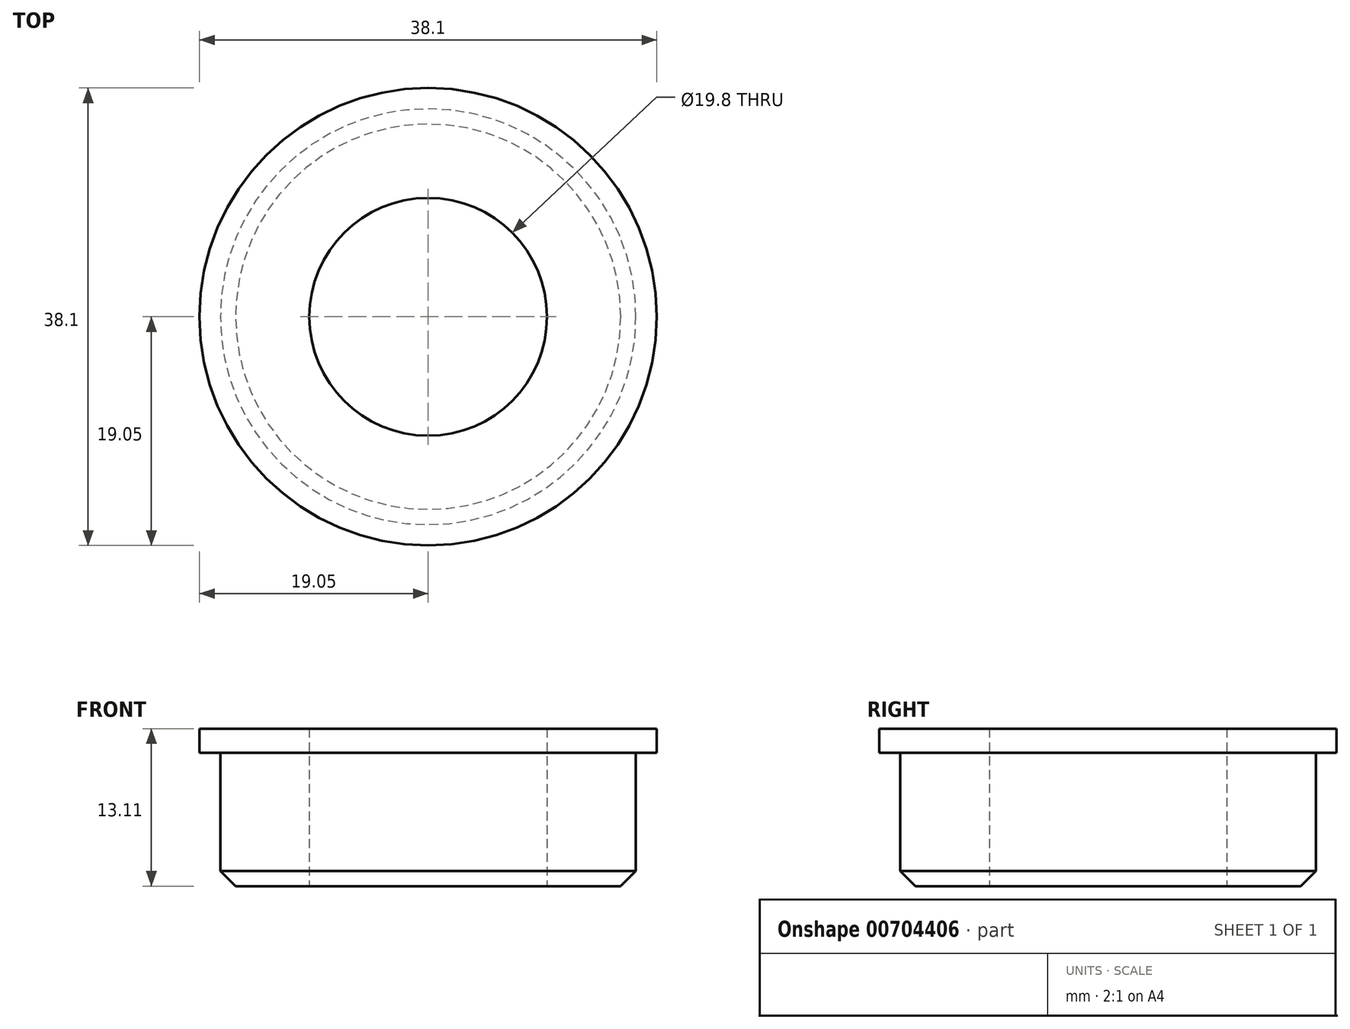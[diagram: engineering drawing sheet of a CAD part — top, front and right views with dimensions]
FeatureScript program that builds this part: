
annotation { "Feature Type Name" : "Feature", "Feature Type Description" : "" }
export const myFeature = defineFeature(function(context is Context, id is Id, definition is map)
    precondition{}
    {
        {
            var Q0;
            Q0=qCreatedBy(makeId("Top.planeOp"),FACE);
            var sketch = newSketch(context, id + "F0", { "sketchPlane" : qUnion([Q0])});
            skCircle(sketch, "E0", {"center": v(0, 0) * mm, "radius": 9.9 * mm});
            skCircle(sketch, "E1", {"center": v(0, 0) * mm, "radius": 17.31 * mm});
            skSolve(sketch);
        }
        {
            var Q0;
            Q0 = qSketchRegion(id + "F0", true);
            extrude(context, id + "F1", {"entities" : qUnion([Q0]), "depth" : 11.1 * mm, "offsetDistance" : 25.4 * mm});
        }
        {
            var Q0;
            Q0=makeQuery(id+"F1.opExtrude","CAP_FACE",FACE,{"disambiguationData":[OSD([sQuery(id+"F0.wireOp",EDGE,"E0"),sQuery(id+"F0.wireOp",EDGE,"E1")])],"isStart":false});
            var sketch = newSketch(context, id + "F2", { "sketchPlane" : qUnion([Q0])});
            skCircle(sketch, "E2", {"center": v(0, 0) * mm, "radius": 19.05 * mm});
            skCircle(sketch, "E3.0", {"center": v(0, 0) * mm, "radius": 9.9 * mm});
            skSolve(sketch);
        }
        {
            var Q0;
            Q0 = qSketchRegion(id + "F2", true);
            extrude(context, id + "F3", {"entities" : qUnion([Q0]), "operationType" : NewBodyOperationType.ADD, "depth" : 2 * mm, "offsetDistance" : 25.4 * mm});
        }
        {
            var Q0;
            Q0=makeQuery(id+"F1.opExtrude","CAP_EDGE",EDGE,{"disambiguationData":[OSD([sQuery(id+"F0.wireOp",EDGE,"E1")])],"isStart":true});
            chamfer(context, id + "F4", {"entities" : qUnion([Q0]), "width" : 1.27 * mm, "tangentPropagation" : true});
        }
    });
